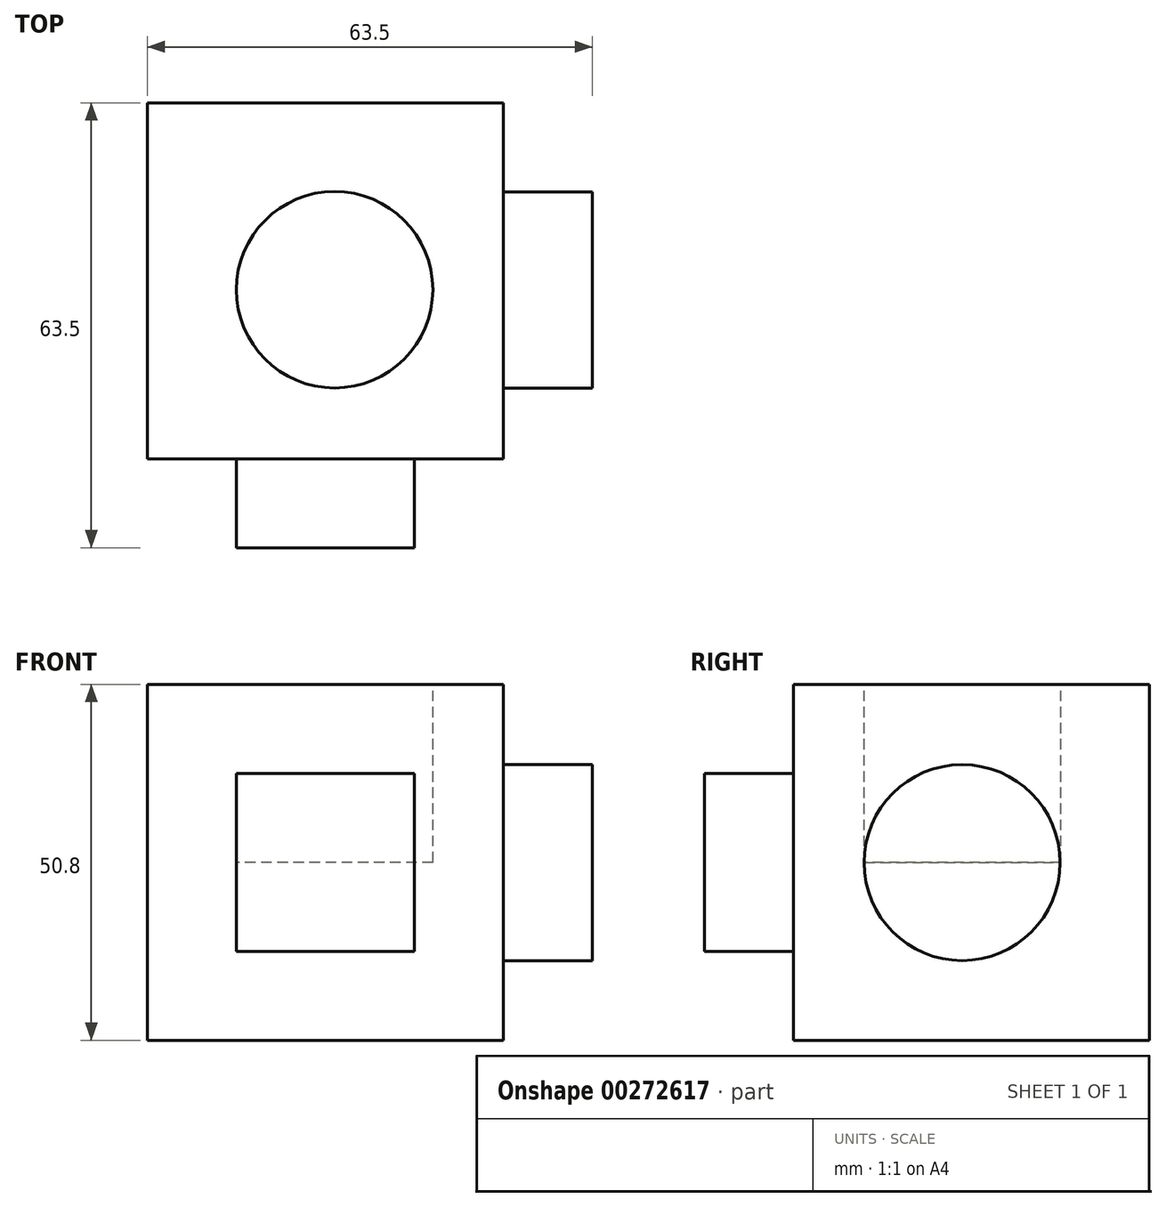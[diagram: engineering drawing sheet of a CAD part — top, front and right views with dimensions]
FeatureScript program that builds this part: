
annotation { "Feature Type Name" : "Feature", "Feature Type Description" : "" }
export const myFeature = defineFeature(function(context is Context, id is Id, definition is map)
    precondition{}
    {
        {
            var Q0;
            Q0=qCreatedBy(makeId("Front.planeOp"),FACE);
            var sketch = newSketch(context, id + "F0", { "sketchPlane" : qUnion([Q0])});
            skLineSegment(sketch, "E0.bottom", {"start": v(-50.8, 50.8) * mm, "end": v(0, 50.8) * mm});
            skLineSegment(sketch, "E0.top", {"start": v(-50.8, 0) * mm, "end": v(0, 0) * mm});
            skLineSegment(sketch, "E0.left", {"start": v(-50.8, 50.8) * mm, "end": v(-50.8, 0) * mm});
            skLineSegment(sketch, "E0.right", {"start": v(0, 50.8) * mm, "end": v(0, 0) * mm});
            skSolve(sketch);
        }
        {
            var Q0;
            Q0 = qSketchRegion(id + "F0", true);
            extrude(context, id + "F1", {"entities" : qUnion([Q0]), "depth" : 50.8 * mm});
        }
        {
            var Q0;
            Q0=makeQuery(id+"F1.opExtrude","CAP_FACE",FACE,{"disambiguationData":[OSD([sQuery(id+"F0.wireOp",EDGE,"E0.bottom"),sQuery(id+"F0.wireOp",EDGE,"E0.top"),sQuery(id+"F0.wireOp",EDGE,"E0.left"),sQuery(id+"F0.wireOp",EDGE,"E0.right")])],"isStart":false});
            var sketch = newSketch(context, id + "F2", { "sketchPlane" : qUnion([Q0])});
            skLineSegment(sketch, "E1.bottom", {"start": v(-38.1, 38.1) * mm, "end": v(-12.7, 38.1) * mm});
            skLineSegment(sketch, "E1.top", {"start": v(-38.1, 12.7) * mm, "end": v(-12.7, 12.7) * mm});
            skLineSegment(sketch, "E1.left", {"start": v(-38.1, 38.1) * mm, "end": v(-38.1, 12.7) * mm});
            skLineSegment(sketch, "E1.right", {"start": v(-12.7, 38.1) * mm, "end": v(-12.7, 12.7) * mm});
            skSolve(sketch);
        }
        {
            var Q0;
            Q0 = qSketchRegion(id + "F2", true);
            extrude(context, id + "F3", {"entities" : qUnion([Q0]), "operationType" : NewBodyOperationType.ADD, "depth" : 12.7 * mm});
        }
        {
            var Q0;
            Q0=makeQuery(id+"F1.opExtrude","SWEPT_FACE",FACE,{"disambiguationData":[OSD([sQuery(id+"F0.wireOp",EDGE,"E0.bottom")])]});
            var sketch = newSketch(context, id + "F4", { "sketchPlane" : qUnion([Q0])});
            skCircle(sketch, "E2", {"center": v(-24.08, -26.69) * mm, "radius": 14.02 * mm});
            skPoint(sketch, "E2.first.point", {"position": v(-20.06, -13.26) * mm});
            skPoint(sketch, "E2.second.point", {"position": v(-36.73, -32.73) * mm});
            skPoint(sketch, "E2.third.point", {"position": v(-35.72, -18.88) * mm});
            skSolve(sketch);
        }
        {
            var Q0;
            Q0=makeQuery(id+"F4.imprint","IMPRINT",FACE,{"disambiguationData":[TD([[makeQuery(id+"F4.imprint","IMPRINT",EDGE,{"derivedFrom":sQuery(id+"F4.wireOp",EDGE,"E2")}),1.0]])]});
            extrude(context, id + "F5", {"entities" : qUnion([Q0]), "operationType" : NewBodyOperationType.REMOVE, "oppositeDirection" : true, "depth" : 25.4 * mm});
        }
        {
            var Q0;
            Q0=makeQuery(id+"F1.opExtrude","SWEPT_FACE",FACE,{"disambiguationData":[OSD([sQuery(id+"F0.wireOp",EDGE,"E0.right")])]});
            var sketch = newSketch(context, id + "F6", { "sketchPlane" : qUnion([Q0])});
            skCircle(sketch, "E3", {"center": v(-26.73, 25.35) * mm, "radius": 13.99 * mm});
            skPoint(sketch, "E3.first.point", {"position": v(-26.73, 39.34) * mm});
            skPoint(sketch, "E3.second.point", {"position": v(-39.15, 18.9) * mm});
            skPoint(sketch, "E3.third.point", {"position": v(-14.32, 18.9) * mm});
            skSolve(sketch);
        }
        {
            var Q0;
            Q0 = qSketchRegion(id + "F6", true);
            extrude(context, id + "F7", {"entities" : qUnion([Q0]), "operationType" : NewBodyOperationType.ADD, "depth" : 12.7 * mm});
        }
    });
